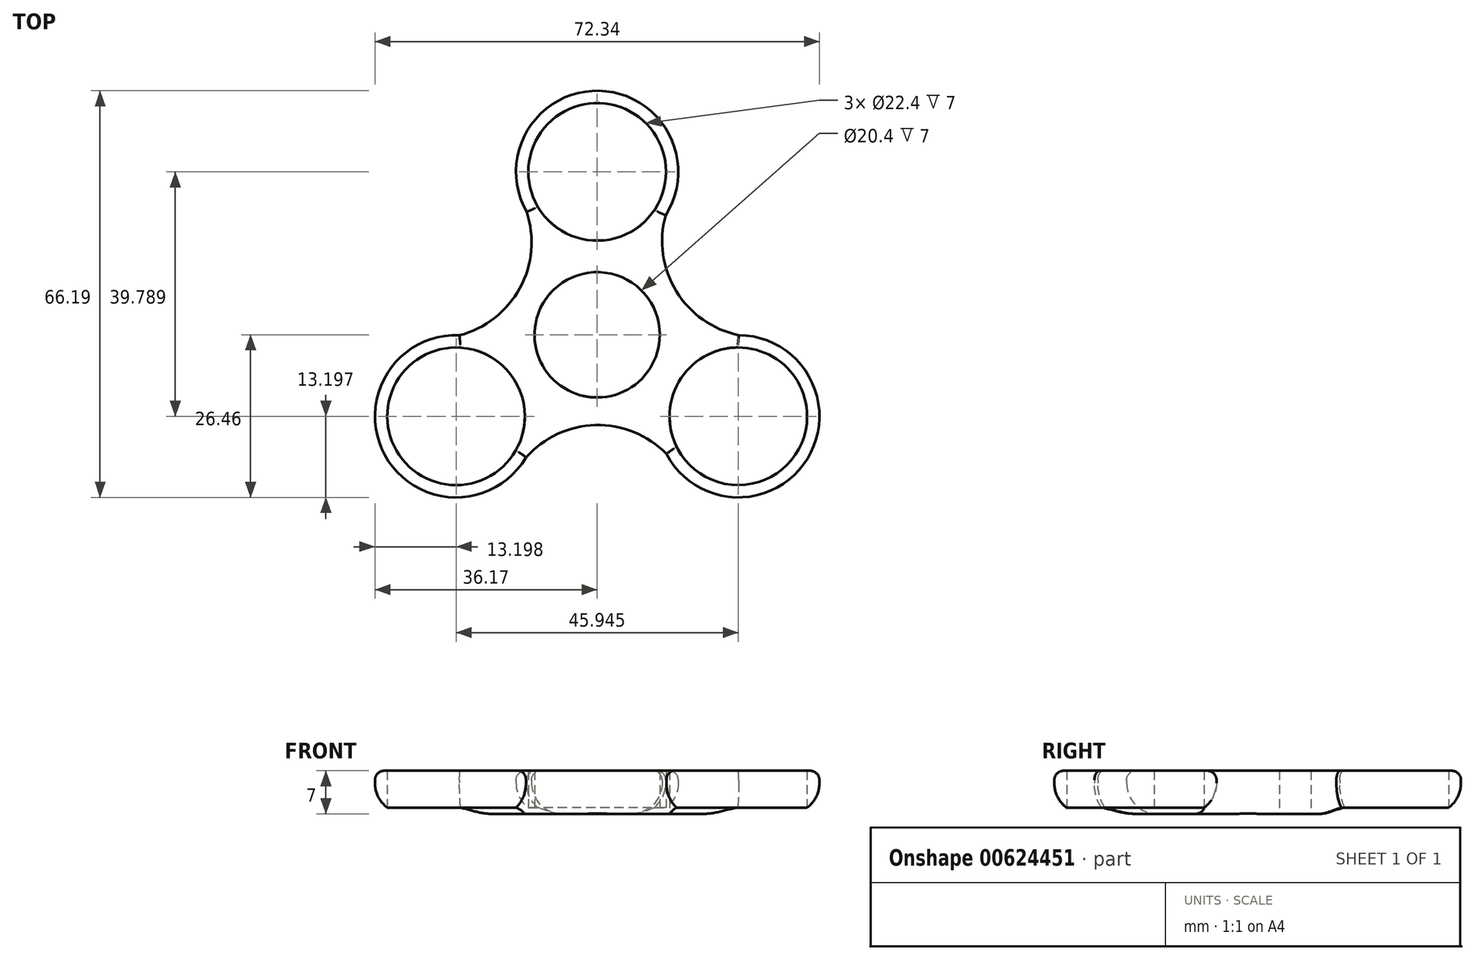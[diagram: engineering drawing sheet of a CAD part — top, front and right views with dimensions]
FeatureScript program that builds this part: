
annotation { "Feature Type Name" : "Feature", "Feature Type Description" : "" }
export const myFeature = defineFeature(function(context is Context, id is Id, definition is map)
    precondition{}
    {
        {
            var Q0;
            Q0=qCreatedBy(makeId("Top.planeOp"),FACE);
            var sketch = newSketch(context, id + "F0", { "sketchPlane" : qUnion([Q0])});
            skCircle(sketch, "E0", {"center": v(0, 0) * mm, "radius": 10.2 * mm});
            skCircle(sketch, "E1", {"center": v(0, 26.53) * mm, "radius": 11.2 * mm});
            skArc(sketch, "E2", {"start": v(11.14, 19.45) * mm, "mid": v(0.32, 39.72) * mm, "end": v(-11.48, 20) * mm});
            skCircle(sketch, "E3.1.0", {"center": v(-22.97, -13.26) * mm, "radius": 11.2 * mm});
            skArc(sketch, "E3.1.1", {"start": v(-22.41, -0.07) * mm, "mid": v(-34.56, -19.58) * mm, "end": v(-11.59, -19.94) * mm});
            skCircle(sketch, "E3.2.0", {"center": v(22.97, -13.26) * mm, "radius": 11.2 * mm});
            skArc(sketch, "E3.2.1", {"start": v(11.27, -19.37) * mm, "mid": v(34.24, -20.14) * mm, "end": v(23.06, -0.06) * mm});
            skArc(sketch, "E4", {"start": v(11.14, 19.45) * mm, "mid": v(12.87, 7.1) * mm, "end": v(23.06, -0.06) * mm});
            skArc(sketch, "E5.1.0", {"start": v(-22.41, -0.07) * mm, "mid": v(-12.6, 7.6) * mm, "end": v(-11.48, 20) * mm});
            skArc(sketch, "E5.2.0", {"start": v(11.27, -19.37) * mm, "mid": v(-0.28, -14.7) * mm, "end": v(-11.59, -19.94) * mm});
            skSolve(sketch);
        }
        {
            var Q0;
            Q0=makeQuery(id+"F0.imprint","IMPRINT",FACE,{"disambiguationData":[TD([[makeQuery(id+"F0.imprint","IMPRINT",EDGE,{"derivedFrom":sQuery(id+"F0.wireOp",EDGE,"E0")}),-1.0]])]});
            extrude(context, id + "F1", {"entities" : qUnion([Q0]), "depth" : 7 * mm, "offsetDistance" : 25 * mm});
        }
        {
            var Q0;
            Q0=makeQuery(id+"F1.opExtrude","CAP_EDGE",EDGE,{"disambiguationData":[OSD([sQuery(id+"F0.wireOp",EDGE,"E3.1.1")])],"isStart":false});
            var Q1;
            Q1=makeQuery(id+"F1.opExtrude","CAP_EDGE",EDGE,{"disambiguationData":[OSD([sQuery(id+"F0.wireOp",EDGE,"E5.1.0")])],"isStart":false});
            var Q2;
            Q2=makeQuery(id+"F1.opExtrude","CAP_EDGE",EDGE,{"disambiguationData":[OSD([sQuery(id+"F0.wireOp",EDGE,"E5.2.0")])],"isStart":false});
            var Q3;
            Q3=makeQuery(id+"F1.opExtrude","CAP_EDGE",EDGE,{"disambiguationData":[OSD([sQuery(id+"F0.wireOp",EDGE,"E2")])],"isStart":false});
            var Q4;
            Q4=makeQuery(id+"F1.opExtrude","CAP_EDGE",EDGE,{"disambiguationData":[OSD([sQuery(id+"F0.wireOp",EDGE,"E4")])],"isStart":false});
            var Q5;
            Q5=makeQuery(id+"F1.opExtrude","CAP_EDGE",EDGE,{"disambiguationData":[OSD([sQuery(id+"F0.wireOp",EDGE,"E3.2.1")])],"isStart":false});
            fillet(context, id + "F2", {"entities" : qUnion([Q0, Q1, Q2, Q3, Q4, Q5]), "radius" : 1.5 * mm, "tangentPropagation" : true, "allowEdgeOverflow" : false});
        }
        {
            var Q0;
            Q0=makeQuery(id+"F1.opExtrude","CAP_EDGE",EDGE,{"disambiguationData":[OSD([sQuery(id+"F0.wireOp",EDGE,"E3.2.1")])],"isStart":true});
            var Q1;
            Q1=makeQuery(id+"F1.opExtrude","CAP_EDGE",EDGE,{"disambiguationData":[OSD([sQuery(id+"F0.wireOp",EDGE,"E5.2.0")])],"isStart":true});
            var Q2;
            Q2=makeQuery(id+"F1.opExtrude","CAP_EDGE",EDGE,{"disambiguationData":[OSD([sQuery(id+"F0.wireOp",EDGE,"E3.1.1")])],"isStart":true});
            var Q3;
            Q3=makeQuery(id+"F1.opExtrude","CAP_EDGE",EDGE,{"disambiguationData":[OSD([sQuery(id+"F0.wireOp",EDGE,"E5.1.0")])],"isStart":true});
            var Q4;
            Q4=makeQuery(id+"F1.opExtrude","CAP_EDGE",EDGE,{"disambiguationData":[OSD([sQuery(id+"F0.wireOp",EDGE,"E2")])],"isStart":true});
            var Q5;
            Q5=makeQuery(id+"F1.opExtrude","CAP_EDGE",EDGE,{"disambiguationData":[OSD([sQuery(id+"F0.wireOp",EDGE,"E4")])],"isStart":true});
            fillet(context, id + "F3", {"entities" : qUnion([Q0, Q1, Q2, Q3, Q4, Q5]), "radius" : 5 * mm, "tangentPropagation" : true, "allowEdgeOverflow" : false});
        }
    });
